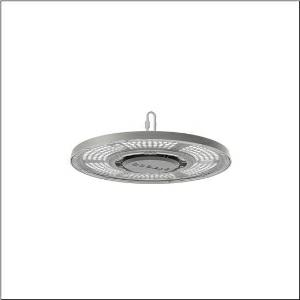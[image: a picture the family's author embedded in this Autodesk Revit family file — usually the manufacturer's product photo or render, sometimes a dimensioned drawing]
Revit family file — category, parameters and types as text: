
# Revit family: highbay_31-s_51hc41da4fmb
name_source: partatom
category: Lighting Fixtures
units: mm (PartAtom-declared; Revit-internal decimal feet)

## family parameters
Cut with Voids When Loaded = No
Host = Face
Light Source = No
Part Type = Normal
Room Calculation Point = No
Round Connector Dimension = Use Diameter
Shared = No

## types (1)
- Highbay 31-S (1 x LED, 14000 lm, 94 W, 4000K)
    Apparent Load = 94 VA
    CIE Flux Codes = 94 98 100 100 100
    Color Rendering = 80
    Color Temperature = 4000K
    Default Elevation = 1800 mm
    Description = Highbay 31-S, high bay luminaire, primary light control with lens, of PC, primary optical cover: cover panel, of PC, transparent, light emission: direct distribution, primary light characteristic: rotationally symmetric, installation type: suspended mounting, surface-mounted, LED, rated luminous flux: 14.000lm, luminous efficacy: 150lm/W, light colour: 840, colour temperature: 4000K, control gear: DALI 2, with cable, 5x 1.0mm², free wire ends, mains connection: 220..240V, AC, 50/60Hz, cable length: 1,5m, rated input power: 94W, housing, rotationally symmetric, of diecast aluminium, powder-coated, grey aluminium (RAL 9007), with hook on luminaire side, incl. screw, diameter: 339mm, protection rating (complete): IP65, insulation class (complete): insulation class I (protective earthing), certification: CE, ENEC, UKCA, protection symbol: D, impact resistance: IK08, permissible operating ambient temperature: -30..+45°C, corresponds to IFS (International Featured Standards) requirements for safety and quality in the food industry, packaging unit: 1 piece
    Height = 141 mm
    Lamp = 1 x LED
    Lamp Light Flux = 14000 lm
    Lamp Power = 94 W
    Lamp count = 1
    Length = 339 mm
    Luminous efficacy = 149 lm/W
    Manufacturer = Siteco
    ModVariant = No
    Model = 51HC41DA4FMB
    Mounting Place = Ceiling
    Mounting Type = Pendant
    Number of Poles = 1
    OnlyDefault = Yes
    Power Factor = 1
    Product Name = Highbay 31-S
    Product group = high bay luminaire
    ProductGroupID = 902
    Protection Class = Protection class I
    Protection Degree = IP 65
    RLX_Detail_Level = 1
    RLX_Emergency_Light_Flux = 0 lm
    RLX_Emergency_Type = 0
    RLX_Emergency_Type_DB = No
    RlxData = <blob elided: 107257 chars, md5=6a9077f5>
    Socket = socket
    Standby Power = 0 W
    System Light Flux = 14000 lm
    System Power = 94 W
    Type Comments = Product without accessories
    Type Image = l_1007237.jpg
    URL = http://relux.com
    VarID = ---
    Voltage = 0 V
    Weight = 0.00 kg
    Width = 0 mm  [stored 0 ft]

note: [stored X ft] marks values corroborated as IEEE doubles in the binary element streams (Revit-internal decimal feet)

## geometry (parser evidence)
native form markers: Blend x4, Sweep x8
no freeform markers — native parametric forms only
